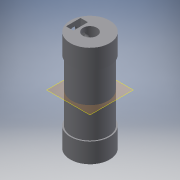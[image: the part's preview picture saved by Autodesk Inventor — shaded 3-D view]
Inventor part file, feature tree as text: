
AUTODESK INVENTOR PART (.ipt)
format: ipt  version: 2016 (Build 200138000, 138)  size: 161,792 bytes
history: native  units: mm
features: sketch x4, extrude x3, projected_geometry x2, revolve x1, plane x1, mirror x1
ambient origin geometry x8: Origin, YZ Plane, XZ Plane, XY Plane, X Axis, Y Axis, Z Axis, Center Point
bodies: Body1 (feature_tree)
feature tree (12):
  revolve  "Revolution1"  [1 undecoded]
  extrude  "Extrusion2"  Depth=41.0mm
  extrude  "Extrusion3"  Depth=5.7mm
  extrude  "Extrusion5"  Depth=3.0mm
  plane  "Work Plane1"
  mirror  "Mirror1"
  sketch  "Sketch1"  dims[d5=8.0mm d6=8.0mm]
  sketch  "Sketch2"  dims[d8=25.0mm d9=41.0mm]
  projected_geometry  "Projected Loop1"
  sketch  "Sketch3"  dims[d10=90.0deg d12=5.7mm]
  projected_geometry  "Projected Loop2"
  sketch  "Sketch4"  dims[d13=20.0mm d14=0.0mm d18=3.0mm d19=5.9mm d20=7.0mm d21=0.0mm d23=3.5mm d26=7.0mm d27=0.0mm d28=2.95mm d29=0.5mm]
note: 1 required parameter value undecoded (feature->parameter linkage not recoverable at this tier; creation-order binding heuristic only, values carry confidence <= 0.55)
